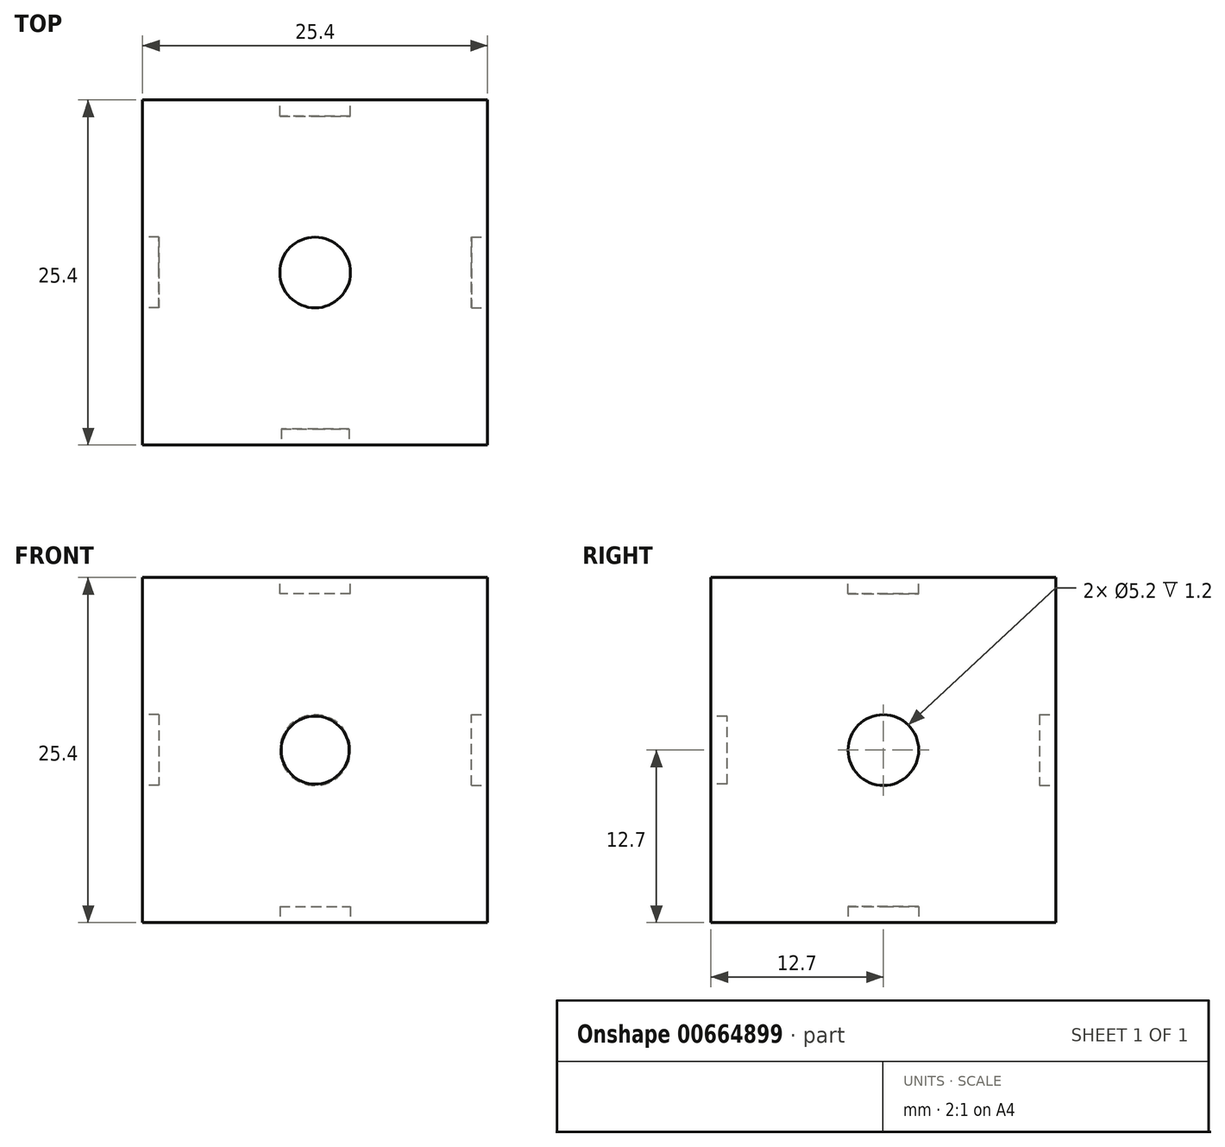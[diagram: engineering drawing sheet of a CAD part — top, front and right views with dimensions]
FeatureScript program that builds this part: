
annotation { "Feature Type Name" : "Feature", "Feature Type Description" : "" }
export const myFeature = defineFeature(function(context is Context, id is Id, definition is map)
    precondition{}
    {
        {
            var Q0;
            Q0=qCreatedBy(makeId("Top.planeOp"),FACE);
            var sketch = newSketch(context, id + "F0", { "sketchPlane" : qUnion([Q0])});
            skLineSegment(sketch, "E0.bottom", {"start": v(12.7, 12.7) * mm, "end": v(-12.7, 12.7) * mm});
            skLineSegment(sketch, "E0.top", {"start": v(12.7, -12.7) * mm, "end": v(-12.7, -12.7) * mm});
            skLineSegment(sketch, "E0.left", {"start": v(12.7, 12.7) * mm, "end": v(12.7, -12.7) * mm});
            skLineSegment(sketch, "E0.right", {"start": v(-12.7, 12.7) * mm, "end": v(-12.7, -12.7) * mm});
            skPoint(sketch, "E0.middle", {"position": v(0, 0) * mm});
            skSolve(sketch);
        }
        {
            var Q0;
            Q0=makeQuery(id+"F0.imprint","IMPRINT",FACE,{"disambiguationData":[TD([[makeQuery(id+"F0.imprint","IMPRINT",EDGE,{"derivedFrom":sQuery(id+"F0.wireOp",EDGE,"E0.bottom")}),1.0]])]});
            extrude(context, id + "F1", {"entities" : qUnion([Q0]), "endBound" : BoundingType.SYMMETRIC, "depth" : 25.4 * mm, "offsetDistance" : 25 * mm});
        }
        {
            var Q0;
            Q0=makeQuery(id+"F1.opExtrude","SWEPT_FACE",FACE,{"disambiguationData":[OSD([sQuery(id+"F0.wireOp",EDGE,"E0.top")])]});
            var sketch = newSketch(context, id + "F2", { "sketchPlane" : qUnion([Q0])});
            skCircle(sketch, "E1", {"center": v(0, 0) * mm, "radius": 2.5 * mm});
            skSolve(sketch);
        }
        {
            var Q0;
            Q0=makeQuery(id+"F1.opExtrude","SWEPT_FACE",FACE,{"disambiguationData":[OSD([sQuery(id+"F0.wireOp",EDGE,"E0.left")])]});
            var sketch = newSketch(context, id + "F3", { "sketchPlane" : qUnion([Q0])});
            skCircle(sketch, "E2", {"center": v(0, 0) * mm, "radius": 2.6 * mm});
            skSolve(sketch);
        }
        {
            var Q0;
            Q0=makeQuery(id+"F1.opExtrude","CAP_FACE",FACE,{"disambiguationData":[OSD([sQuery(id+"F0.wireOp",EDGE,"E0.bottom"),sQuery(id+"F0.wireOp",EDGE,"E0.top"),sQuery(id+"F0.wireOp",EDGE,"E0.left"),sQuery(id+"F0.wireOp",EDGE,"E0.right")])],"isStart":false});
            var sketch = newSketch(context, id + "F4", { "sketchPlane" : qUnion([Q0])});
            skCircle(sketch, "E3", {"center": v(0, 0) * mm, "radius": 2.6 * mm});
            skSolve(sketch);
        }
        {
            var Q0;
            Q0=makeQuery(id+"F1.opExtrude","SWEPT_FACE",FACE,{"disambiguationData":[OSD([sQuery(id+"F0.wireOp",EDGE,"E0.right")])]});
            var sketch = newSketch(context, id + "F5", { "sketchPlane" : qUnion([Q0])});
            skCircle(sketch, "E4", {"center": v(0, 0) * mm, "radius": 2.6 * mm});
            skSolve(sketch);
        }
        {
            var Q0;
            Q0=makeQuery(id+"F1.opExtrude","CAP_FACE",FACE,{"disambiguationData":[OSD([sQuery(id+"F0.wireOp",EDGE,"E0.bottom"),sQuery(id+"F0.wireOp",EDGE,"E0.top"),sQuery(id+"F0.wireOp",EDGE,"E0.left"),sQuery(id+"F0.wireOp",EDGE,"E0.right")])],"isStart":true});
            var sketch = newSketch(context, id + "F6", { "sketchPlane" : qUnion([Q0])});
            skCircle(sketch, "E5", {"center": v(0, 0) * mm, "radius": 2.6 * mm});
            skSolve(sketch);
        }
        {
            var Q0;
            Q0=makeQuery(id+"F1.opExtrude","SWEPT_FACE",FACE,{"disambiguationData":[OSD([sQuery(id+"F0.wireOp",EDGE,"E0.bottom")])]});
            var sketch = newSketch(context, id + "F7", { "sketchPlane" : qUnion([Q0])});
            skCircle(sketch, "E6", {"center": v(0, 0) * mm, "radius": 2.6 * mm});
            skSolve(sketch);
        }
        {
            var Q0;
            Q0=makeQuery(id+"F7.imprint","IMPRINT",FACE,{"disambiguationData":[TD([[makeQuery(id+"F7.imprint","IMPRINT",EDGE,{"derivedFrom":sQuery(id+"F7.wireOp",EDGE,"E6")}),1.0]])]});
            extrude(context, id + "F8", {"entities" : qUnion([Q0]), "operationType" : NewBodyOperationType.REMOVE, "oppositeDirection" : true, "depth" : 1.2 * mm, "offsetDistance" : 25 * mm});
        }
        {
            var Q0;
            Q0=makeQuery(id+"F6.imprint","IMPRINT",FACE,{"disambiguationData":[TD([[makeQuery(id+"F6.imprint","IMPRINT",EDGE,{"derivedFrom":sQuery(id+"F6.wireOp",EDGE,"E5")}),1.0]])]});
            extrude(context, id + "F9", {"entities" : qUnion([Q0]), "operationType" : NewBodyOperationType.REMOVE, "oppositeDirection" : true, "depth" : 1.2 * mm, "offsetDistance" : 25 * mm});
        }
        {
            var Q0;
            Q0=makeQuery(id+"F5.imprint","IMPRINT",FACE,{"disambiguationData":[TD([[makeQuery(id+"F5.imprint","IMPRINT",EDGE,{"derivedFrom":sQuery(id+"F5.wireOp",EDGE,"E4")}),1.0]])]});
            extrude(context, id + "F10", {"entities" : qUnion([Q0]), "operationType" : NewBodyOperationType.REMOVE, "oppositeDirection" : true, "depth" : 1.2 * mm, "offsetDistance" : 25 * mm});
        }
        {
            var Q0;
            Q0=makeQuery(id+"F4.imprint","IMPRINT",FACE,{"disambiguationData":[TD([[makeQuery(id+"F4.imprint","IMPRINT",EDGE,{"derivedFrom":sQuery(id+"F4.wireOp",EDGE,"E3")}),1.0]])]});
            extrude(context, id + "F11", {"entities" : qUnion([Q0]), "operationType" : NewBodyOperationType.REMOVE, "oppositeDirection" : true, "depth" : 1.2 * mm, "offsetDistance" : 25 * mm});
        }
        {
            var Q0;
            Q0=makeQuery(id+"F2.imprint","IMPRINT",FACE,{"disambiguationData":[TD([[makeQuery(id+"F2.imprint","IMPRINT",EDGE,{"derivedFrom":sQuery(id+"F2.wireOp",EDGE,"E1")}),1.0]])]});
            extrude(context, id + "F12", {"entities" : qUnion([Q0]), "operationType" : NewBodyOperationType.REMOVE, "oppositeDirection" : true, "depth" : 1.2 * mm, "offsetDistance" : 25 * mm});
        }
        {
            var Q0;
            Q0=makeQuery(id+"F3.imprint","IMPRINT",FACE,{"disambiguationData":[TD([[makeQuery(id+"F3.imprint","IMPRINT",EDGE,{"derivedFrom":sQuery(id+"F3.wireOp",EDGE,"E2")}),1.0]])]});
            extrude(context, id + "F13", {"entities" : qUnion([Q0]), "operationType" : NewBodyOperationType.REMOVE, "oppositeDirection" : true, "depth" : 1.2 * mm, "offsetDistance" : 25 * mm});
        }
    });
